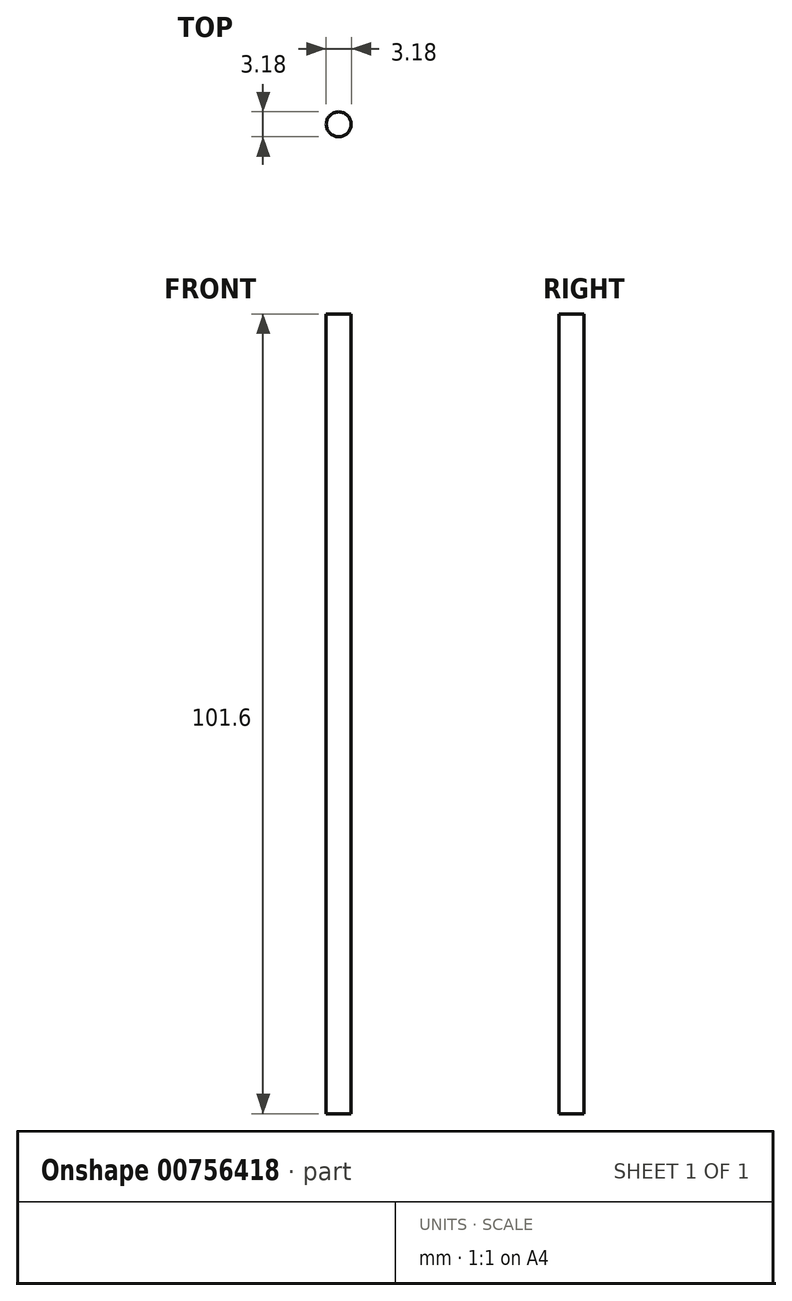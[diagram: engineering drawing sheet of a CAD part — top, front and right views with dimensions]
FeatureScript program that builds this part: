
annotation { "Feature Type Name" : "Feature", "Feature Type Description" : "" }
export const myFeature = defineFeature(function(context is Context, id is Id, definition is map)
    precondition{}
    {
        {
            var Q0;
            Q0=qCreatedBy(makeId("Top.planeOp"),FACE);
            var sketch = newSketch(context, id + "F0", { "sketchPlane" : qUnion([Q0])});
            skCircle(sketch, "E0", {"center": v(0, 0) * mm, "radius": 1.59 * mm});
            skSolve(sketch);
        }
        {
            var Q0;
            Q0 = qSketchRegion(id + "F0", true);
            extrude(context, id + "F1", {"entities" : qUnion([Q0]), "depth" : 101.6 * mm, "offsetDistance" : 25.4 * mm});
        }
    });
